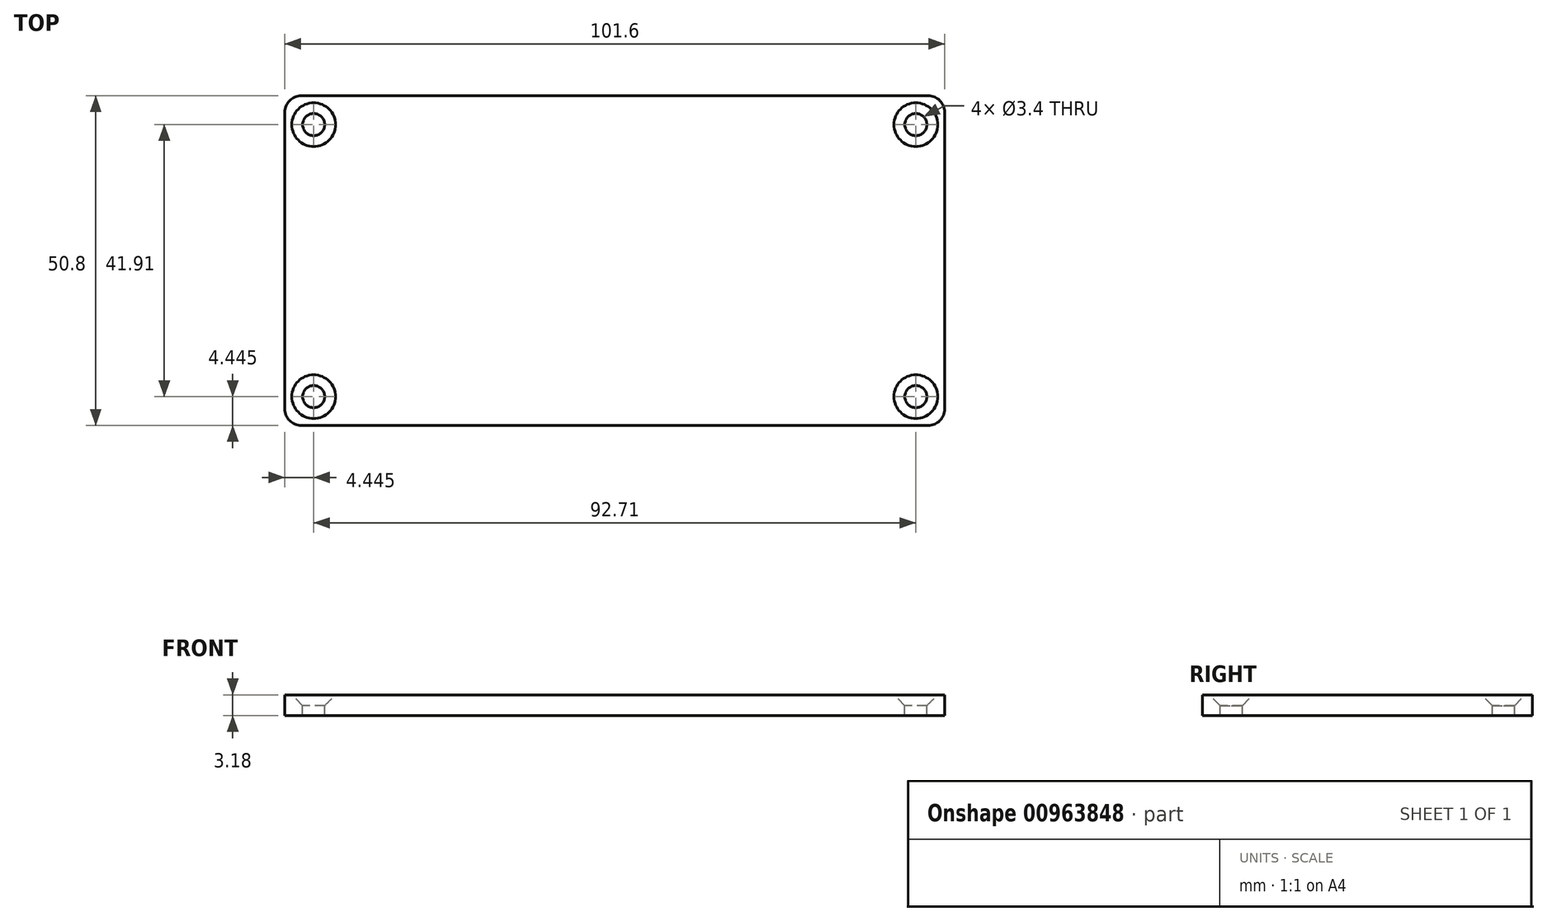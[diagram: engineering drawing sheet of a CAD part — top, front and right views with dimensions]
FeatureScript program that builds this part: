
annotation { "Feature Type Name" : "Feature", "Feature Type Description" : "" }
export const myFeature = defineFeature(function(context is Context, id is Id, definition is map)
    precondition{}
    {
        {
            var Q0;
            Q0=qCreatedBy(makeId("Top.planeOp"),FACE);
            var sketch = newSketch(context, id + "F0", { "sketchPlane" : qUnion([Q0])});
            skLineSegment(sketch, "E0.bottom", {"start": v(50.8, -25.4) * mm, "end": v(-50.8, -25.4) * mm});
            skLineSegment(sketch, "E0.top", {"start": v(50.8, 25.4) * mm, "end": v(-50.8, 25.4) * mm});
            skLineSegment(sketch, "E0.left", {"start": v(50.8, -25.4) * mm, "end": v(50.8, 25.4) * mm});
            skLineSegment(sketch, "E0.right", {"start": v(-50.8, -25.4) * mm, "end": v(-50.8, 25.4) * mm});
            skPoint(sketch, "E0.middle", {"position": v(0, 0) * mm});
            skSolve(sketch);
        }
        {
            var Q0;
            Q0=makeQuery(id+"F0.imprint","IMPRINT",FACE,{"disambiguationData":[TD([[makeQuery(id+"F0.imprint","IMPRINT",EDGE,{"derivedFrom":sQuery(id+"F0.wireOp",EDGE,"E0.bottom")}),-1.0]])]});
            extrude(context, id + "F1", {"entities" : qUnion([Q0]), "oppositeDirection" : true, "depth" : 3.17 * mm, "offsetDistance" : 25.4 * mm});
        }
        {
            var Q0;
            Q0=makeQuery(id+"F1.opExtrude","SWEPT_EDGE",EDGE,{"disambiguationData":[OSD([sQuery(id+"F0.wireOp",EDGE,"E0.bottom"),sQuery(id+"F0.wireOp",EDGE,"E0.right")])]});
            var Q1;
            Q1=makeQuery(id+"F1.opExtrude","SWEPT_EDGE",EDGE,{"disambiguationData":[OSD([sQuery(id+"F0.wireOp",EDGE,"E0.bottom"),sQuery(id+"F0.wireOp",EDGE,"E0.left")])]});
            var Q2;
            Q2=makeQuery(id+"F1.opExtrude","SWEPT_EDGE",EDGE,{"disambiguationData":[OSD([sQuery(id+"F0.wireOp",EDGE,"E0.top"),sQuery(id+"F0.wireOp",EDGE,"E0.left")])]});
            var Q3;
            Q3=makeQuery(id+"F1.opExtrude","SWEPT_EDGE",EDGE,{"disambiguationData":[OSD([sQuery(id+"F0.wireOp",EDGE,"E0.top"),sQuery(id+"F0.wireOp",EDGE,"E0.right")])]});
            fillet(context, id + "F2", {"entities" : qUnion([Q0, Q1, Q2, Q3]), "radius" : 2.54 * mm, "tangentPropagation" : true, "allowEdgeOverflow" : false});
        }
        {
            var Q0;
            Q0=makeQuery(id+"F1.opExtrude","CAP_FACE",FACE,{"disambiguationData":[OSD([sQuery(id+"F0.wireOp",EDGE,"E0.bottom"),sQuery(id+"F0.wireOp",EDGE,"E0.top"),sQuery(id+"F0.wireOp",EDGE,"E0.left"),sQuery(id+"F0.wireOp",EDGE,"E0.right")])],"isStart":true});
            var sketch = newSketch(context, id + "F3", { "sketchPlane" : qUnion([Q0])});
            skPoint(sketch, "E1", {"position": v(-46.36, 20.95) * mm});
            skPoint(sketch, "E2", {"position": v(46.36, 20.96) * mm});
            skPoint(sketch, "E3", {"position": v(46.36, -20.95) * mm});
            skPoint(sketch, "E4", {"position": v(-46.36, -20.95) * mm});
            skSolve(sketch);
        }
        {
            var Q0;
            Q0=sQuery(id+"F3.wireOp",VERTEX,"E1");
            var Q1;
            Q1=sQuery(id+"F3.wireOp",VERTEX,"E2");
            var Q2;
            Q2=sQuery(id+"F3.wireOp",VERTEX,"E3");
            var Q3;
            Q3=sQuery(id+"F3.wireOp",VERTEX,"E4");
            var Q4;
            Q4=makeQuery(id+"F1.opExtrude","SWEPT_BODY",BODY,{"disambiguationData":[OSD([sQuery(id+"F0.wireOp",EDGE,"E0.bottom"),sQuery(id+"F0.wireOp",EDGE,"E0.top"),sQuery(id+"F0.wireOp",EDGE,"E0.left"),sQuery(id+"F0.wireOp",EDGE,"E0.right")])]});
            hole(context, id + "F4", {"style" : HoleStyle.C_SINK, "endStyle" : HoleEndStyle.THROUGH, "standardTappedOrClearance" : lookupTablePath({ "fit" : "Normal", "standard" : "ISO", "size" : "M3", "type" : "Clearance" }), "standardBlindInLast" : lookupTablePath({ "fit" : "Normal", "standard" : "ISO", "engagement" : "75%", "pitch" : "0.5 mm", "size" : "M3", "type" : "Clearance & tapped" }), "holeDiameter" : 3.4 * mm, "cSinkDiameter" : 6.72 * mm, "cSinkAngle" : 90 * degree, "majorDiameter" : 6.35 * mm, "isTappedThrough" : true, "tappedDepth" : 3.96 * mm, "tapClearance" : 3, "startFromSketch" : true, "locations" : qUnion([Q0, Q1, Q2, Q3]), "scope" : qUnion([Q4])});
        }
    });
